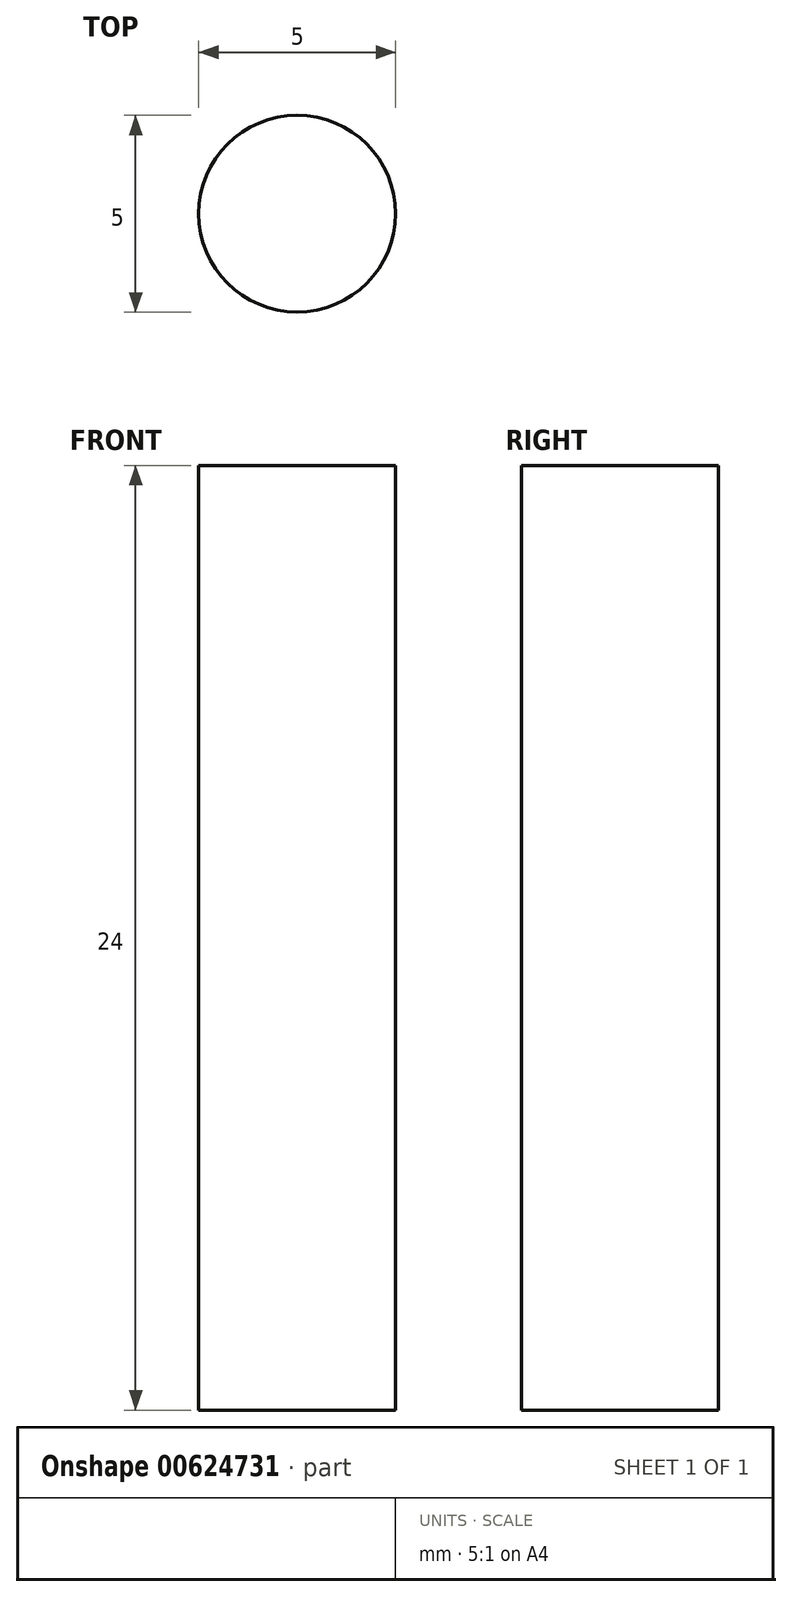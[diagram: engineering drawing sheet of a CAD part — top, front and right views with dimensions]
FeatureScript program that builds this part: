
annotation { "Feature Type Name" : "Feature", "Feature Type Description" : "" }
export const myFeature = defineFeature(function(context is Context, id is Id, definition is map)
    precondition{}
    {
        {
            var Q0;
            Q0=qCreatedBy(makeId("Top.planeOp"),FACE);
            var sketch = newSketch(context, id + "F0", { "sketchPlane" : qUnion([Q0])});
            skCircle(sketch, "E0", {"center": v(0, 0) * mm, "radius": 2.5 * mm});
            skSolve(sketch);
        }
        {
            var Q0;
            Q0 = qSketchRegion(id + "F0", true);
            extrude(context, id + "F1", {"entities" : qUnion([Q0]), "depth" : 24 * mm, "offsetDistance" : 25 * mm});
        }
    });
